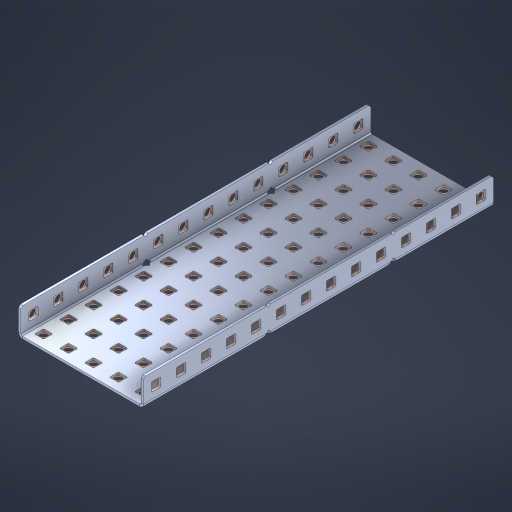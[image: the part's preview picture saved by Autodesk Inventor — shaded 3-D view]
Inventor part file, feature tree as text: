
AUTODESK INVENTOR PART (.ipt)
format: ipt  version: 2023 (Build 270158000, 158)  size: 1,274,880 bytes
history: native  units: in
note: dims shown in document units (in); Inventor stores cm internally (conversion verified against a paired STEP export)
features: other x103, extrude x97, sheet_metal_op x10, sketch x8, mirror x1, pattern_linear x1, chamfer x1
ambient origin geometry x8: Origin, YZ Plane, XZ Plane, XY Plane, X Axis, Y Axis, Z Axis, Center Point
bodies: Solid1 (feature_tree), Body (feature_tree)
feature tree (221):
  other  "Flange Pattern Plane"
  sheet_metal_op  "Flange Pattern"
  sheet_metal_op  "Body Pattern"
  other  "Arc Length"
  mirror  "Notch Mirror"
  pattern_linear  "Notch Pattern"  Spacing1=0.1875in  [1 undecoded]
  chamfer  "End Chamfer"
  extrude  "Half Cut"  Depth=0.0469in
  sketch  "Sketch1"  dims[d0=2.5in]
  other  "Plate1"
  sketch  "Sketch2"  dims[d1=7.0in]
  other  "Plate2"
  sheet_metal_op  "Bend1"
  sheet_metal_op  "Corner1"
  sketch  "Sketch3"  dims[d2=0.0469in]
  other  "Flange Pattern Sketch"
  sketch  "Sketch7"  dims[d3=0.0469in]
  other  "Srf1"
  other  "Srf2"
  sketch  "Sketch8"  dims[d4=0.0234in]
  sketch  "Sketch9"  dims[d5=0.0938in]
  other  "Srf91"
  sheet_metal_op  "Body Pattern Sketch"
  other  "Srf92"
  sketch  "Sketch13"  dims[d6=0.0469in]
  sketch  "Sketch14"  dims[d7=0.5in d8=90.0deg d9=0.0312in d10=0.1875in d11=0.0469in d12=0.0469in d16=0.182in d17=0.02in d18=0.0469in d19=0.0in d20=0.25in d21=0.25in d46=0.172in d47=1.0in d48=0.0in d49=0.182in d50=0.02in d51=0.25in d52=0.25in d53=0.0469in d54=0.0in d55=0.172in d56=1.0in d57=0.0in d60=5.5118in d62=0.5in d63=1.9685in d65=0.5in d85=0.1227in d86=0.1659in d88=0.04in d89=0.0469in d90=0.0in d91=0.04in d92=0.0491in d95=2.5in d96=0.04in d97=0.25in d98=45.0deg d101=0.0in d102=2.497in d131=2.5in d132=5.5118in d134=0.5in d139=0.5in]
  other  "Srf856"
  other  "Srf1310"
  other  "Srf1311"
  other  "Srf1312"
  other  "Srf1376"
  other  "Srf1377"
  other  "Srf1728"
  other  "Srf1755"
  other  "Srf1878"
  other  "Srf1879"
  other  "Srf1880"
  other  "Srf1881"
  other  "Srf1882"
  other  "Srf1883"
  other  "Srf1884"
  other  "Srf1885"
  other  "Srf1886"
  other  "Srf1887"
  other  "Srf1888"
  other  "Srf1889"
  other  "Srf1890"
  other  "Srf1891"
  other  "Srf1892"
  other  "Srf1893"
  other  "Srf1894"
  other  "Srf1895"
  other  "Srf1896"
  other  "Srf1897"
  other  "Srf1898"
  other  "Srf1899"
  other  "Srf1942"
  other  "Srf1943"
  other  "Srf1944"
  other  "Srf1945"
  other  "Srf1946"
  other  "Srf1947"
  other  "Srf1948"
  other  "Srf1949"
  other  "Srf1950"
  other  "Srf1951"
  other  "Srf1952"
  other  "Srf1953"
  other  "Srf1954"
  other  "Srf1955"
  other  "Srf1956"
  other  "Srf1957"
  other  "Srf1958"
  other  "Srf1959"
  other  "Srf1960"
  other  "Srf1961"
  other  "Srf1962"
  other  "Srf1963"
  other  "Srf1964"
  other  "Srf1965"
  other  "Srf1966"
  other  "Srf1967"
  other  "Srf1968"
  other  "Srf1969"
  other  "Srf1970"
  other  "Srf2146"
  other  "Srf2147"
  other  "Srf2148"
  other  "Srf2149"
  other  "Srf2150"
  other  "Srf2151"
  other  "Srf2152"
  other  "Srf2153"
  other  "Srf2154"
  other  "Srf2155"
  other  "Srf2156"
  other  "Srf2157"
  other  "Srf2158"
  other  "Srf2159"
  other  "Srf2160"
  other  "Srf2161"
  other  "Srf2162"
  other  "Srf2163"
  other  "Srf2164"
  other  "Srf2165"
  other  "Srf2166"
  other  "Srf2167"
  other  "Srf2168"
  other  "Srf2169"
  other  "Srf2170"
  other  "Srf2171"
  other  "Srf2172"
  other  "Srf2173"
  other  "Srf2174"
  other  "Srf2175"
  other  "Srf2176"
  other  "Srf2177"
  other  "Srf2178"
  other  "Srf2179"
  other  "Srf2180"
  sheet_metal_op  "Flange Stamp"
  sheet_metal_op  "Flange Circle"
  sheet_metal_op  "Body Stamp"
  sheet_metal_op  "Body Circle"
  sheet_metal_op  "Notch"
  extrude  "ExtrusionSrf2"  Depth=0.0469in
  extrude  "ExtrusionSrf92"  Depth=2.5in
  extrude  "ExtrusionSrf856"  Depth=0.02in
  extrude  "ExtrusionSrf1310"  Depth=0.0469in
  extrude  "ExtrusionSrf1311"  TaperAngle=0.0deg  [1 undecoded]
  extrude  "ExtrusionSrf1312"  Depth=0.25in
  extrude  "ExtrusionSrf1376"  Depth=0.25in
  extrude  "ExtrusionSrf1377"  Depth=2.5in
  extrude  "ExtrusionSrf1728"  Depth=2.5in TaperAngle=0.0deg
  extrude  "ExtrusionSrf1755"  Depth=2.5in
  extrude  "ExtrusionSrf1878"  Depth=0.02in
  extrude  "ExtrusionSrf1879"  Depth=0.25in
  extrude  "ExtrusionSrf1880"  Depth=0.25in
  extrude  "ExtrusionSrf1881"  Depth=0.0469in
  extrude  "ExtrusionSrf1882"  TaperAngle=0.0deg  [1 undecoded]
  extrude  "ExtrusionSrf1883"  Depth=2.5in
  extrude  "ExtrusionSrf1884"  Depth=2.5in TaperAngle=0.0deg
  extrude  "ExtrusionSrf1885"  Depth=2.5in
  extrude  "ExtrusionSrf1886"  Depth=2.5in
  extrude  "ExtrusionSrf1887"  Depth=2.5in
  extrude  "ExtrusionSrf1888"  Depth=2.5in
  extrude  "ExtrusionSrf1889"  Depth=2.5in
  extrude  "ExtrusionSrf1890"  Depth=0.0469in
  extrude  "ExtrusionSrf1891"  TaperAngle=0.0deg  [1 undecoded]
  extrude  "ExtrusionSrf1892"  Depth=2.5in
  extrude  "ExtrusionSrf1893"  Depth=2.5in
  extrude  "ExtrusionSrf1894"  Depth=2.5in
  extrude  "ExtrusionSrf1895"  Depth=0.25in TaperAngle=45.0deg
  extrude  "ExtrusionSrf1896"  TaperAngle=0.0deg  [1 undecoded]
  extrude  "ExtrusionSrf1897"  Depth=2.5in
  extrude  "ExtrusionSrf1898"  Depth=2.5in
  extrude  "ExtrusionSrf1899"  Depth=2.5in
  extrude  "ExtrusionSrf1942"  Depth=2.5in
  extrude  "ExtrusionSrf1943"  Depth=2.5in
  extrude  "ExtrusionSrf1944"  [1 undecoded]
  extrude  "ExtrusionSrf1945"  [1 undecoded]
  extrude  "ExtrusionSrf1946"  [1 undecoded]
  extrude  "ExtrusionSrf1947"  [1 undecoded]
  extrude  "ExtrusionSrf1948"  [1 undecoded]
  extrude  "ExtrusionSrf1949"  [1 undecoded]
  extrude  "ExtrusionSrf1950"  [1 undecoded]
  extrude  "ExtrusionSrf1951"  [1 undecoded]
  extrude  "ExtrusionSrf1952"  [1 undecoded]
  extrude  "ExtrusionSrf1953"  [1 undecoded]
  extrude  "ExtrusionSrf1954"  [1 undecoded]
  extrude  "ExtrusionSrf1955"  [1 undecoded]
  extrude  "ExtrusionSrf1956"  [1 undecoded]
  extrude  "ExtrusionSrf1957"  [1 undecoded]
  extrude  "ExtrusionSrf1958"  [1 undecoded]
  extrude  "ExtrusionSrf1959"  [1 undecoded]
  extrude  "ExtrusionSrf1960"  [1 undecoded]
  extrude  "ExtrusionSrf1961"  [1 undecoded]
  extrude  "ExtrusionSrf1962"  [1 undecoded]
  extrude  "ExtrusionSrf1963"  [1 undecoded]
  extrude  "ExtrusionSrf1964"  [1 undecoded]
  extrude  "ExtrusionSrf1965"  [1 undecoded]
  extrude  "ExtrusionSrf1966"  [1 undecoded]
  extrude  "ExtrusionSrf1967"  [1 undecoded]
  extrude  "ExtrusionSrf1968"  [1 undecoded]
  extrude  "ExtrusionSrf1969"  [1 undecoded]
  extrude  "ExtrusionSrf1970"  [1 undecoded]
  extrude  "ExtrusionSrf2146"  [1 undecoded]
  extrude  "ExtrusionSrf2147"  [1 undecoded]
  extrude  "ExtrusionSrf2148"  [1 undecoded]
  extrude  "ExtrusionSrf2149"  [1 undecoded]
  extrude  "ExtrusionSrf2150"  [1 undecoded]
  extrude  "ExtrusionSrf2151"  [1 undecoded]
  extrude  "ExtrusionSrf2152"  [1 undecoded]
  extrude  "ExtrusionSrf2153"  [1 undecoded]
  extrude  "ExtrusionSrf2154"  [1 undecoded]
  extrude  "ExtrusionSrf2155"  [1 undecoded]
  extrude  "ExtrusionSrf2156"  [1 undecoded]
  extrude  "ExtrusionSrf2157"  [1 undecoded]
  extrude  "ExtrusionSrf2158"  [1 undecoded]
  extrude  "ExtrusionSrf2159"  [1 undecoded]
  extrude  "ExtrusionSrf2160"  [1 undecoded]
  extrude  "ExtrusionSrf2161"  [1 undecoded]
  extrude  "ExtrusionSrf2162"  [1 undecoded]
  extrude  "ExtrusionSrf2163"  [1 undecoded]
  extrude  "ExtrusionSrf2164"  [1 undecoded]
  extrude  "ExtrusionSrf2165"  [1 undecoded]
  extrude  "ExtrusionSrf2166"  [1 undecoded]
  extrude  "ExtrusionSrf2167"  [1 undecoded]
  extrude  "ExtrusionSrf2168"  [1 undecoded]
  extrude  "ExtrusionSrf2169"  [1 undecoded]
  extrude  "ExtrusionSrf2170"  [1 undecoded]
  extrude  "ExtrusionSrf2171"  [1 undecoded]
  extrude  "ExtrusionSrf2172"  [1 undecoded]
  extrude  "ExtrusionSrf2173"  [1 undecoded]
  extrude  "ExtrusionSrf2174"  [1 undecoded]
  extrude  "ExtrusionSrf2175"  [1 undecoded]
  extrude  "ExtrusionSrf2176"  [1 undecoded]
  extrude  "ExtrusionSrf2177"  [1 undecoded]
  extrude  "ExtrusionSrf2178"  [1 undecoded]
  extrude  "ExtrusionSrf2179"  [1 undecoded]
  extrude  "ExtrusionSrf2180"  [1 undecoded]
note: 67 required parameter values undecoded (feature->parameter linkage not recoverable at this tier; creation-order binding heuristic only, values carry confidence <= 0.55)
